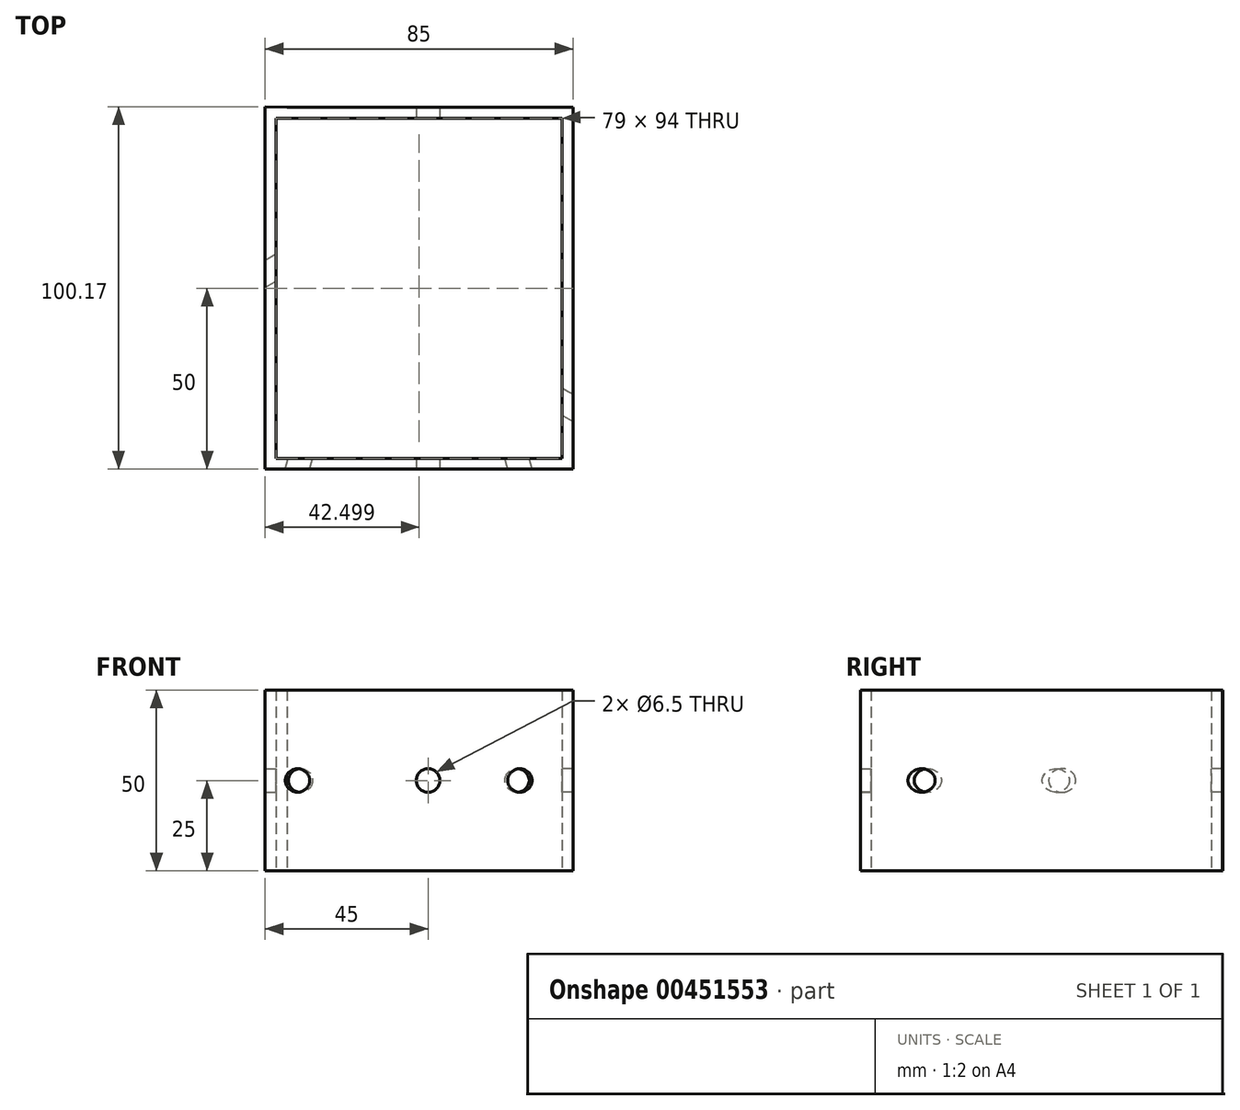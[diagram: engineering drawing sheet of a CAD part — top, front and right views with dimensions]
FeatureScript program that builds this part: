
annotation { "Feature Type Name" : "Feature", "Feature Type Description" : "" }
export const myFeature = defineFeature(function(context is Context, id is Id, definition is map)
    precondition{}
    {
        {
            var Q0;
            Q0=qCreatedBy(makeId("Top.planeOp"),FACE);
            var sketch = newSketch(context, id + "F0", { "sketchPlane" : qUnion([Q0])});
            skLineSegment(sketch, "E0", {"start": v(0, 0) * mm, "end": v(0, -20) * mm});
            skLineSegment(sketch, "E1", {"start": v(0, -20) * mm, "end": v(0, -70) * mm});
            skLineSegment(sketch, "E2", {"start": v(0, -20) * mm, "end": v(43.3, -45) * mm});
            skLineSegment(sketch, "E3", {"start": v(0, -20) * mm, "end": v(17.32, -30) * mm});
            skLineSegment(sketch, "E4", {"start": v(17.32, -30) * mm, "end": v(29.39, -75.04) * mm});
            skLineSegment(sketch, "E5", {"start": v(0, 0) * mm, "end": v(0, 20) * mm});
            skLineSegment(sketch, "E6", {"start": v(0, 20) * mm, "end": v(0, 70) * mm});
            skLineSegment(sketch, "E7", {"start": v(0, 20) * mm, "end": v(-17.32, 10) * mm});
            skLineSegment(sketch, "E8", {"start": v(-17.32, 10) * mm, "end": v(-61.05, -14.24) * mm});
            skLineSegment(sketch, "E9", {"start": v(-17.32, 10) * mm, "end": v(-43.55, -81.44) * mm});
            skSolve(sketch);
        }
        {
            var Q0;
            Q0=qCreatedBy(makeId("Top.planeOp"),FACE);
            var sketch = newSketch(context, id + "F1", { "sketchPlane" : qUnion([Q0])});
            skLineSegment(sketch, "E10.top", {"start": v(-40, -60) * mm, "end": v(40, -60) * mm});
            skLineSegment(sketch, "E10.right", {"start": v(40, 39.97) * mm, "end": v(40, -60) * mm});
            skPoint(sketch, "E10.middle", {"position": v(0, 0) * mm});
            skLineSegment(sketch, "E11", {"start": v(-39, 39.97) * mm, "end": v(40, 39.97) * mm});
            skPoint(sketch, "E12.orphan", {"position": v(-40, 60) * mm});
            skPoint(sketch, "E13.orphan", {"position": v(40, 60) * mm});
            skLineSegment(sketch, "E14", {"start": v(-39, 39.97) * mm, "end": v(-36, 39.97) * mm});
            skLineSegment(sketch, "E15", {"start": v(-37, -57) * mm, "end": v(37, -57) * mm});
            skLineSegment(sketch, "E16", {"start": v(37, -57) * mm, "end": v(37, 37) * mm});
            skLineSegment(sketch, "E17", {"start": v(37, 37) * mm, "end": v(-37, 37) * mm});
            skLineSegment(sketch, "E18", {"start": v(-40, -60) * mm, "end": v(-45, -60) * mm});
            skLineSegment(sketch, "E19", {"start": v(-45, -60) * mm, "end": v(-45, 40.17) * mm});
            skLineSegment(sketch, "E20", {"start": v(-45, 40.17) * mm, "end": v(-39, 39.97) * mm});
            skLineSegment(sketch, "E21", {"start": v(-45, 40.17) * mm, "end": v(-42, 40.07) * mm});
            skLineSegment(sketch, "E22", {"start": v(-42, 37) * mm, "end": v(-42, -57) * mm});
            skLineSegment(sketch, "E23", {"start": v(-37, 37) * mm, "end": v(-42, 37) * mm});
            skLineSegment(sketch, "E24", {"start": v(-37, -57) * mm, "end": v(-42, -57) * mm});
            skPoint(sketch, "E25.orphan", {"position": v(-42, -60) * mm});
            skSolve(sketch);
        }
        {
            var Q0;
            Q0 = qSketchRegion(id + "F1", true);
            extrude(context, id + "F2", {"entities" : qUnion([Q0]), "depth" : 25 * mm});
        }
        {
            var Q0;
            Q0 = qSketchRegion(id + "F1", true);
            extrude(context, id + "F3", {"entities" : qUnion([Q0]), "operationType" : NewBodyOperationType.ADD, "oppositeDirection" : true, "depth" : 25 * mm});
        }
        {
            var Q0;
            Q0=qCreatedBy(makeId("Front.planeOp"),FACE);
            cPlane(context, id + "F4", {"entities" : qUnion([Q0]), "cplaneType" : CPlaneType.OFFSET, "offset" : 20 * mm, "width" : 150 * mm, "height" : 150 * mm});
        }
        {
            var Q0;
            Q0=qCreatedBy(id+"F4.planeOp",FACE);
            var sketch = newSketch(context, id + "F5", { "sketchPlane" : qUnion([Q0])});
            skLineSegment(sketch, "E26", {"start": v(0, 0) * mm, "end": v(0, -43.62) * mm});
            skSolve(sketch);
        }
        {
            var Q0;
            Q0=qCreatedBy(id+"F4.planeOp",FACE);
            var Q1;
            Q1 = qBodyType(qCreatedBy(id + "F5" ,EDGE), BodyType.WIRE);
            cPlane(context, id + "F6", {"entities" : qUnion([Q0, Q1]), "cplaneType" : CPlaneType.LINE_ANGLE, "offset" : 25 * mm, "angle" : 120 * degree, "width" : 150 * mm, "height" : 150 * mm});
        }
        {
            var Q0;
            Q0=qCreatedBy(id+"F6.planeOp",FACE);
            cPlane(context, id + "F7", {"entities" : qUnion([Q0]), "cplaneType" : CPlaneType.OFFSET, "offset" : 20 * mm, "width" : 150 * mm, "height" : 150 * mm});
        }
        {
            var Q0;
            Q0=qCreatedBy(id+"F7.planeOp",FACE);
            var sketch = newSketch(context, id + "F8", { "sketchPlane" : qUnion([Q0])});
            skLineSegment(sketch, "E27", {"start": v(-17.32, 0) * mm, "end": v(-17.32, -100) * mm});
            skSolve(sketch);
        }
        {
            var Q0;
            Q0=qCreatedBy(id+"F7.planeOp",FACE);
            var Q1;
            Q1 = qBodyType(qCreatedBy(id + "F8" ,EDGE), BodyType.WIRE);
            cPlane(context, id + "F9", {"entities" : qUnion([Q0, Q1]), "cplaneType" : CPlaneType.LINE_ANGLE, "offset" : 25 * mm, "angle" : 45 * degree, "width" : 150 * mm, "height" : 150 * mm});
        }
        {
            var Q0;
            Q0=qCreatedBy(id+"F9.planeOp",FACE);
            var sketch = newSketch(context, id + "F10", { "sketchPlane" : qUnion([Q0])});
            skCircle(sketch, "E28", {"center": v(-8.97, 0) * mm, "radius": 3.25 * mm});
            skSolve(sketch);
        }
        {
            var Q0;
            Q0 = qSketchRegion(id + "F10", true);
            extrude(context, id + "F11", {"entities" : qUnion([Q0]), "operationType" : NewBodyOperationType.REMOVE, "oppositeDirection" : true, "depth" : 50 * mm});
        }
        {
            var Q0;
            Q0=qCreatedBy(id+"F7.planeOp",FACE);
            var sketch = newSketch(context, id + "F12", { "sketchPlane" : qUnion([Q0])});
            skCircle(sketch, "E29", {"center": v(-17.32, 0) * mm, "radius": 3.25 * mm});
            skSolve(sketch);
        }
        {
            var Q0;
            Q0 = qSketchRegion(id + "F12", true);
            extrude(context, id + "F13", {"entities" : qUnion([Q0]), "operationType" : NewBodyOperationType.REMOVE, "depth" : 50 * mm});
        }
        {
            var Q0;
            {var subQ0=sQuery(id+"F1.wireOp",EDGE,"E18");var subQ1=sQuery(id+"F1.wireOp",EDGE,"E10.top");Q0=makeQuery(id+"F3.boolean.opBoolean","MERGE",FACE,{"derivedFrom":[makeQuery(id+"F2.opExtrude","SWEPT_FACE",FACE,{"disambiguationData":[OSD([subQ1,subQ0])]}),makeQuery(id+"F3.opExtrude","SWEPT_FACE",FACE,{"disambiguationData":[OSD([subQ1,subQ0])]})]});}
            var sketch = newSketch(context, id + "F14", { "sketchPlane" : qUnion([Q0])});
            skCircle(sketch, "E30", {"center": v(0, 0) * mm, "radius": 3.25 * mm});
            skSolve(sketch);
        }
        {
            var Q0;
            Q0 = qSketchRegion(id + "F14", true);
            extrude(context, id + "F15", {"entities" : qUnion([Q0]), "operationType" : NewBodyOperationType.REMOVE, "oppositeDirection" : true, "depth" : 120 * mm});
        }
        {
            var Q0;
            Q0=qCreatedBy(makeId("Front.planeOp"),FACE);
            cPlane(context, id + "F16", {"entities" : qUnion([Q0]), "cplaneType" : CPlaneType.OFFSET, "offset" : 20 * mm, "oppositeDirection" : true, "width" : 150 * mm, "height" : 150 * mm});
        }
        {
            var Q0;
            Q0=qCreatedBy(id+"F16.planeOp",FACE);
            var sketch = newSketch(context, id + "F17", { "sketchPlane" : qUnion([Q0])});
            skLineSegment(sketch, "E31", {"start": v(0, 0) * mm, "end": v(0, 58.81) * mm});
            skSolve(sketch);
        }
        {
            var Q0;
            Q0=qCreatedBy(id+"F16.planeOp",FACE);
            var Q1;
            Q1 = qBodyType(qCreatedBy(id + "F17" ,EDGE), BodyType.WIRE);
            cPlane(context, id + "F18", {"entities" : qUnion([Q0, Q1]), "cplaneType" : CPlaneType.LINE_ANGLE, "offset" : 25 * mm, "angle" : 60 * degree, "oppositeDirection" : true, "width" : 150 * mm, "height" : 150 * mm});
        }
        {
            var Q0;
            Q0=qCreatedBy(id+"F18.planeOp",FACE);
            cPlane(context, id + "F19", {"entities" : qUnion([Q0]), "cplaneType" : CPlaneType.OFFSET, "offset" : 20 * mm, "oppositeDirection" : true, "width" : 150 * mm, "height" : 150 * mm});
        }
        {
            var Q0;
            Q0=qCreatedBy(id+"F19.planeOp",FACE);
            var sketch = newSketch(context, id + "F20", { "sketchPlane" : qUnion([Q0])});
            skLineSegment(sketch, "E32", {"start": v(17.32, 0) * mm, "end": v(17.32, -41.26) * mm});
            skSolve(sketch);
        }
        {
            var Q0;
            Q0=qCreatedBy(id+"F19.planeOp",FACE);
            var Q1;
            Q1 = qBodyType(qCreatedBy(id + "F20" ,EDGE), BodyType.WIRE);
            cPlane(context, id + "F21", {"entities" : qUnion([Q0, Q1]), "cplaneType" : CPlaneType.LINE_ANGLE, "offset" : 25 * mm, "angle" : 45 * degree, "oppositeDirection" : true, "width" : 150 * mm, "height" : 150 * mm});
        }
        {
            var Q0;
            Q0=qCreatedBy(id+"F21.planeOp",FACE);
            var sketch = newSketch(context, id + "F22", { "sketchPlane" : qUnion([Q0])});
            skCircle(sketch, "E33", {"center": v(-19.32, 0) * mm, "radius": 3.25 * mm});
            skSolve(sketch);
        }
        {
            var Q0;
            Q0 = qSketchRegion(id + "F22", true);
            extrude(context, id + "F23", {"entities" : qUnion([Q0]), "operationType" : NewBodyOperationType.REMOVE, "depth" : 100 * mm});
        }
        {
            var Q0;
            Q0=qCreatedBy(id+"F19.planeOp",FACE);
            var sketch = newSketch(context, id + "F24", { "sketchPlane" : qUnion([Q0])});
            skCircle(sketch, "E34", {"center": v(17.32, 0) * mm, "radius": 3.25 * mm});
            skSolve(sketch);
        }
        {
            var Q0;
            Q0 = qSketchRegion(id + "F24", true);
            extrude(context, id + "F25", {"entities" : qUnion([Q0]), "operationType" : NewBodyOperationType.REMOVE, "oppositeDirection" : true, "depth" : 100 * mm});
        }
    });
